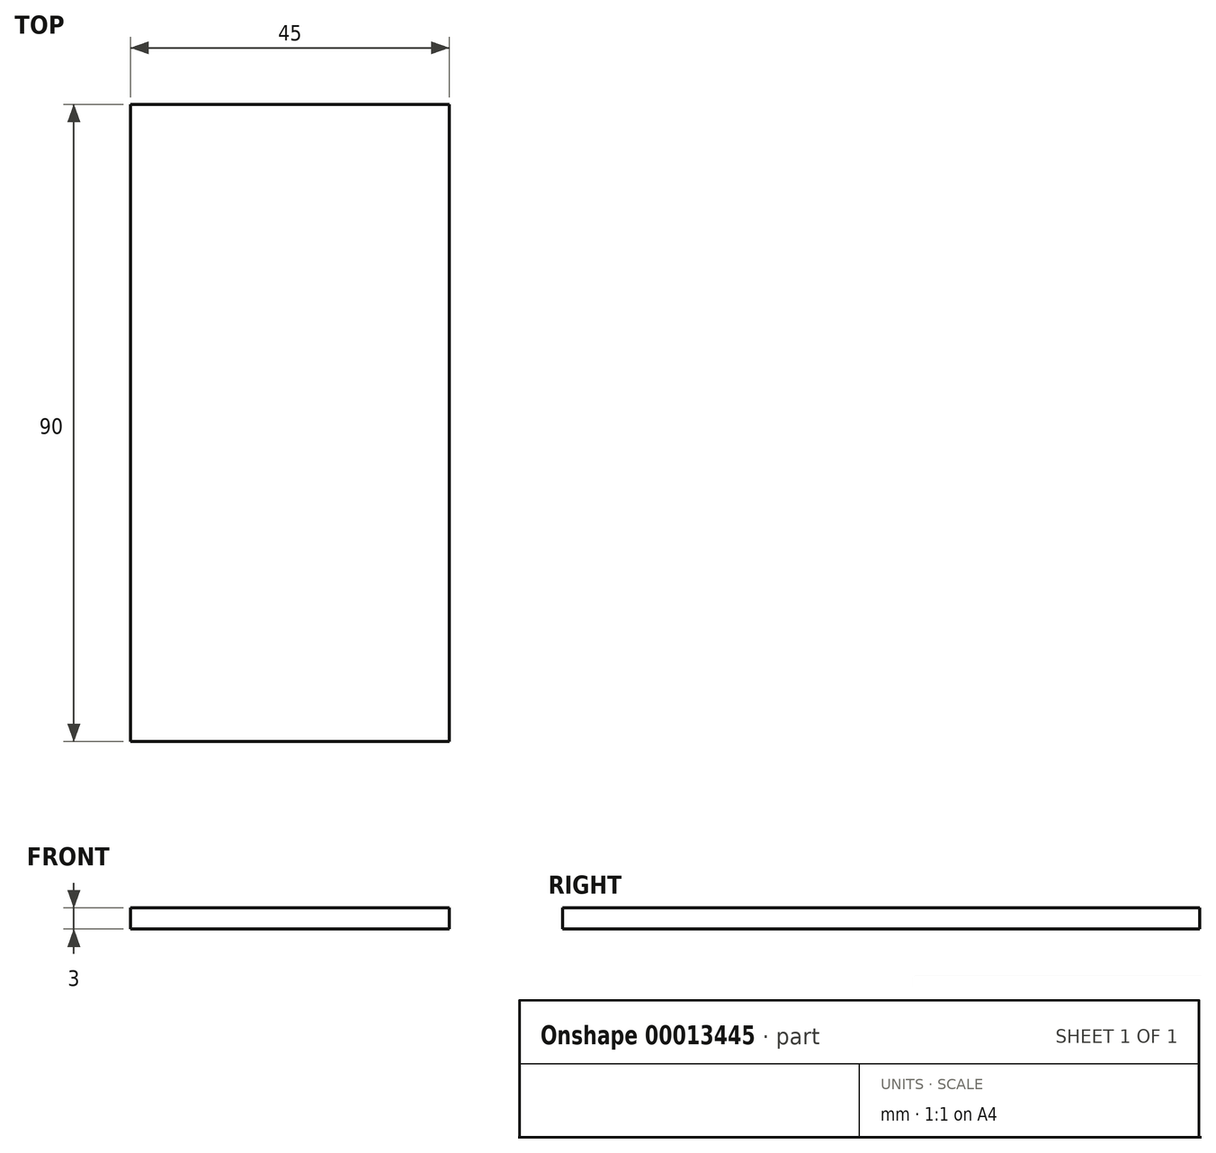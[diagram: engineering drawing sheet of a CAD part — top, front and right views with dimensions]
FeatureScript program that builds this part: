
annotation { "Feature Type Name" : "Feature", "Feature Type Description" : "" }
export const myFeature = defineFeature(function(context is Context, id is Id, definition is map)
    precondition{}
    {
        {
            var Q0;
            Q0=qCreatedBy(makeId("Top.planeOp"),FACE);
            var sketch = newSketch(context, id + "F0", { "sketchPlane" : qUnion([Q0])});
            skLineSegment(sketch, "E0.bottom", {"start": v(-39.32, 73.29) * mm, "end": v(5.68, 73.29) * mm});
            skLineSegment(sketch, "E0.top", {"start": v(-39.32, -16.71) * mm, "end": v(5.68, -16.71) * mm});
            skLineSegment(sketch, "E0.left", {"start": v(-39.32, 73.29) * mm, "end": v(-39.32, -16.71) * mm});
            skLineSegment(sketch, "E0.right", {"start": v(5.68, 73.29) * mm, "end": v(5.68, -16.71) * mm});
            skSolve(sketch);
        }
        {
            var Q0;
            Q0=qSketchRegion(id+"F0",true);
            extrude(context, id + "F1", {"entities" : qUnion([Q0]), "depth" : 3 * mm});
        }
    });
